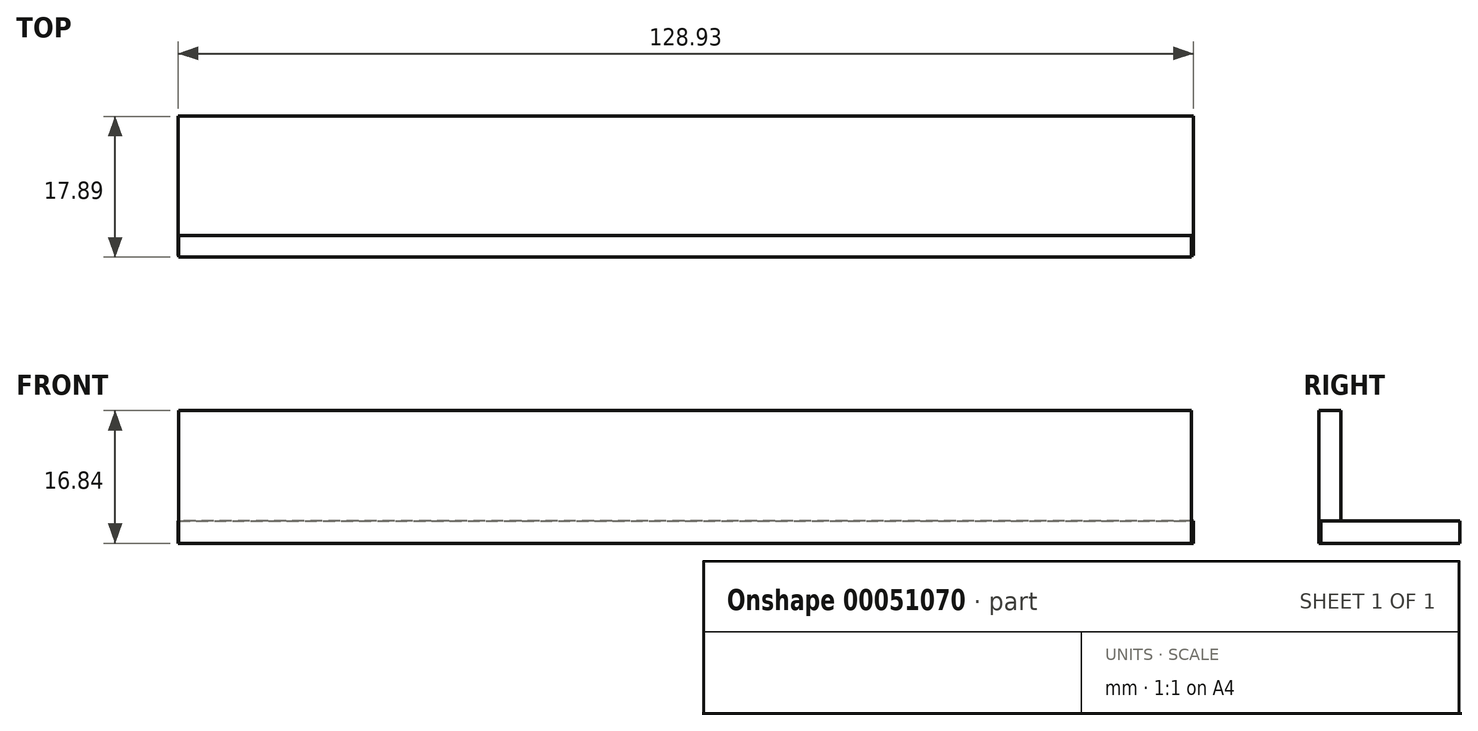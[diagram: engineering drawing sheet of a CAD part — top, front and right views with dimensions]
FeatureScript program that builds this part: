
annotation { "Feature Type Name" : "Feature", "Feature Type Description" : "" }
export const myFeature = defineFeature(function(context is Context, id is Id, definition is map)
    precondition{}
    {
        {
            var Q0;
            Q0=qCreatedBy(makeId("Top.planeOp"),FACE);
            var sketch = newSketch(context, id + "F0", { "sketchPlane" : qUnion([Q0])});
            skLineSegment(sketch, "E0.bottom", {"start": v(-58.9, 54.81) * mm, "end": v(70.03, 54.81) * mm});
            skLineSegment(sketch, "E0.top", {"start": v(-58.9, 37.14) * mm, "end": v(70.03, 37.14) * mm});
            skLineSegment(sketch, "E0.left", {"start": v(-58.9, 54.81) * mm, "end": v(-58.9, 37.14) * mm});
            skLineSegment(sketch, "E0.right", {"start": v(70.03, 54.81) * mm, "end": v(70.03, 37.14) * mm});
            skSolve(sketch);
        }
        {
            var Q0;
            Q0=makeQuery(id+"F0.imprint","IMPRINT",FACE,{"disambiguationData":[TD([[makeQuery(id+"F0.imprint","IMPRINT",EDGE,{"derivedFrom":sQuery(id+"F0.wireOp",EDGE,"E0.bottom")}),-1.0]])]});
            extrude(context, id + "F1", {"entities" : qUnion([Q0]), "depth" : 2.82 * mm});
        }
        {
            var Q0;
            Q0=qCreatedBy(makeId("Top.planeOp"),FACE);
            var sketch = newSketch(context, id + "F2", { "sketchPlane" : qUnion([Q0])});
            skLineSegment(sketch, "E1.bottom", {"start": v(-58.83, 36.92) * mm, "end": v(69.8, 36.92) * mm});
            skLineSegment(sketch, "E1.top", {"start": v(-58.83, 39.7) * mm, "end": v(69.8, 39.7) * mm});
            skLineSegment(sketch, "E1.left", {"start": v(-58.83, 36.92) * mm, "end": v(-58.83, 39.7) * mm});
            skLineSegment(sketch, "E1.right", {"start": v(69.8, 36.92) * mm, "end": v(69.8, 39.7) * mm});
            skLineSegment(sketch, "E2.bottom", {"start": v(-59, 54.77) * mm, "end": v(70.14, 54.77) * mm});
            skLineSegment(sketch, "E2.top", {"start": v(-59, 52) * mm, "end": v(70.14, 52) * mm});
            skLineSegment(sketch, "E2.left", {"start": v(-59, 54.77) * mm, "end": v(-59, 52) * mm});
            skLineSegment(sketch, "E2.right", {"start": v(70.14, 54.77) * mm, "end": v(70.14, 52) * mm});
            skSolve(sketch);
        }
        {
            var Q0;
            Q0=makeQuery(id+"F2.imprint","IMPRINT",FACE,{"disambiguationData":[TD([[makeQuery(id+"F2.imprint","IMPRINT",EDGE,{"derivedFrom":sQuery(id+"F2.wireOp",EDGE,"E1.bottom")}),1.0]])]});
            extrude(context, id + "F3", {"entities" : qUnion([Q0]), "operationType" : NewBodyOperationType.ADD, "depth" : 16.83 * mm});
        }
    });
